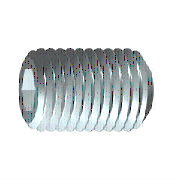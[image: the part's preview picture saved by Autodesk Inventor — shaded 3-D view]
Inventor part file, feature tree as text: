
AUTODESK INVENTOR PART (.ipt)
format: ipt  version: 2020 (Build 240168000, 168)  size: 174,080 bytes
history: native  units: mm (DEFAULTED — no unit token found)
features: sketch x2, extrude x1, other x1, plane x1
ambient origin geometry x8: Origin, YZ Plane, XZ Plane, XY Plane, X Axis, Y Axis, Z Axis, Center Point
bodies: Solid1 (feature_tree), Body (feature_tree)
feature tree (5):
  extrude  "Slot"  TaperAngle=60.0deg  [1 undecoded]
  other  "Work Axis1"
  plane  "Work Plane1"
  sketch  "Sketch1"  dims[d0=2.5mm d1=60.0deg]
  sketch  "Sketch2"  dims[d2=4.0mm d3=2.309401mm d6=90.0deg d4=10.0mm d5=60.0deg d7=2.0mm d8=2.5mm d9=0.0mm d10=1.0mm d11=45.0deg d12=0.429415mm d13=45.0deg d14=10.0mm d15=0.0mm d16=0.0mm d33=1.0mm d34=0.429415mm d35=0.0mm d37=0.0mm]
note: 1 required parameter value undecoded (feature->parameter linkage not recoverable at this tier; creation-order binding heuristic only, values carry confidence <= 0.55)
